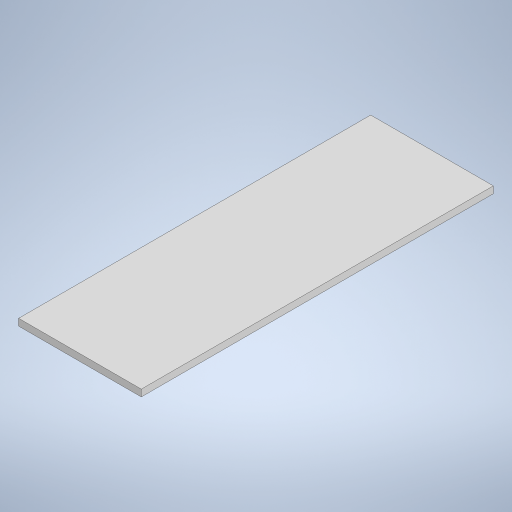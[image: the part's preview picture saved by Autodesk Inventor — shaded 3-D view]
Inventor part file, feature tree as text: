
AUTODESK INVENTOR PART (.ipt)
format: ipt  version: 2024 (Build 280153000, 153)  size: 511,488 bytes
history: native  units: mm
features: extrude x1, sketch x1
ambient origin geometry x8: Origin, YZ Plane, XZ Plane, XY Plane, X Axis, Y Axis, Z Axis, Center Point
bodies: Solid1 (feature_tree)
feature tree (2):
  extrude  "Extrusion1"  Depth=36.097mm
  sketch  "Sketch1"  dims[d0=103.6mm d1=36.097mm d2=2.0mm d3=0.0mm]
